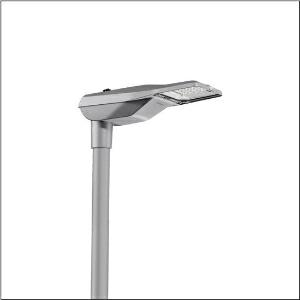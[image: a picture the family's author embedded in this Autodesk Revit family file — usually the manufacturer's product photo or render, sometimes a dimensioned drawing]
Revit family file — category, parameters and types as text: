
# Revit family: streetlight_sl_21_iq_micro___st1_0ab_5xe1m31v08db_4fb3
name_source: partatom
category: Lighting Fixtures
units: mm (PartAtom-declared; Revit-internal decimal feet)

## family parameters
Cut with Voids When Loaded = No
Host = Face
Light Source = No
Part Type = Normal
Room Calculation Point = No
Round Connector Dimension = Use Diameter
Shared = No

## types (1)
- --- (1 x LED, 4490 lm, 39.1 W, 3000K)
    Apparent Load = 39 VA
    CIE Flux Codes = 38 73 97 100 100
    Color Rendering = 70
    Color Temperature = 3000K
    Default Elevation = 1800 mm
    Description = Streetlight SL 21 iQ micro, mast luminaire, primary light control with lens, of PMMA, primary optical cover: cover, of toughened safety glass, transparent, light distribution: ST1.0aB, light emission: direct distribution, primary light characteristic: asymmetric, installation type: post-top, side-entry, LED, High Power LED, rated luminous flux: 4.490lm, luminous efficacy: 115lm/W, light colour: 730, colour temperature: 3000K, control: pre-setting: logarithmic dimming characteristic, Street-Remote, Auto-Match, Temp-Guard, Lumen-Switch, Night-Set, Smart-Wire, Light-Fading, Desk-Remote (wireless, voltage-free reading and setting of iQ features in the workshop via application-optimized NFC function/RFID function), optimised constant luminous flux control (CLO 2.0), mains connection: 220..240V, AC, 50/60Hz, start of lifetime: 39W, end of service life: 41W, reduction: 17W, luminaire housing, of diecast aluminium, powder-coated, Siteco® metallic grey (DB 702S), corrosivity category C5 mid according to DIN EN ISO 12944, please order mast flange separately, inclination adjustable: 0°, 5°, 10°, 15°, sealing non-destructively replaceable, multi-level sealing system, length: 528mm, width: 235mm, height: 110mm, mast flange for spigot size: 42mm (side-entry): 5XC10008XM4, 60/48mm (side-entry/post-top): 5XC10108XM2, 76/60mm (side-entry/post-top): 5XC10108XM1, Smart Interface above, protection rating (complete): IP66, insulation class (complete): insulation class II (safety insulation), certification: CE, ENEC, ENEC+, VDE, impact resistance: IK09, permissible operating ambient temperature for outdoor applications: -40..+50°C, standard-compliant lighting for roads and squares, packaging unit: 1 piece

Light Distribution: ST1.0aB
    Height = 110 mm
    Lamp = 1 x LED
    Lamp Light Flux = 4490 lm
    Lamp Power = 39.1 W
    Lamp count = 1
    Length = 528 mm
    Luminous efficacy = 115 lm/W
    Manufacturer = Siteco
    ModVariant = No
    Model = 5XE1M31V08DB
    Number of Poles = 1
    OnlyDefault = Yes
    Power Factor = 1
    Product Name = Streetlight SL 21 iQ micro | ST1.0aB
    Product group = mast luminaire | pylon top
    ProductGroupID = 6100
    Protection Class = Protection class II
    Protection Degree = IP 66
    RLX_Detail_Level = 1
    RLX_Emergency_Light_Flux = 0 lm
    RLX_Emergency_Type = 0
    RLX_Emergency_Type_DB = No
    RlxData = <blob elided: 98433 chars, md5=b83ddb08>
    Socket = socket
    Standby Power = 0 W
    System Light Flux = 4490 lm
    System Power = 39 W
    Type Comments = factory setting: luminous flux: 100 % | dim-lin: 254 | 765 mA
    Type Image = l_1277292.jpg
    URL = http://relux.com
    VarID = @adj_081557
    Voltage = 0 V
    Weight = 0.00 kg
    Width = 235 mm

## geometry (parser evidence)
native form markers: Blend x4, Sweep x11
no freeform markers — native parametric forms only
